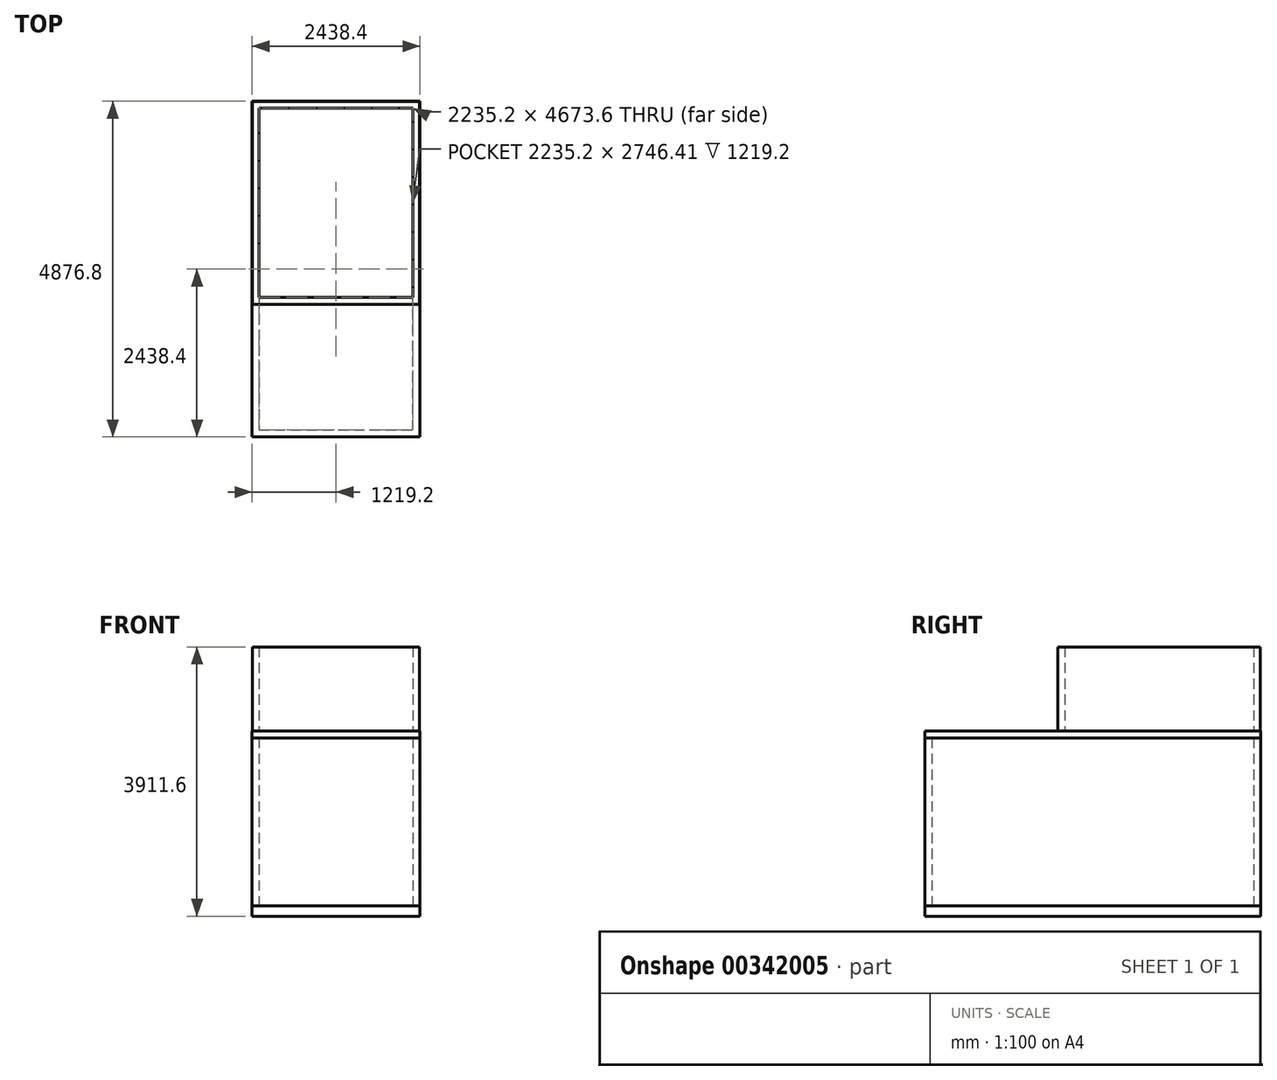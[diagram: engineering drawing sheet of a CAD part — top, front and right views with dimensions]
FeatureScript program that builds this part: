
annotation { "Feature Type Name" : "Feature", "Feature Type Description" : "" }
export const myFeature = defineFeature(function(context is Context, id is Id, definition is map)
    precondition{}
    {
        {
            var Q0;
            Q0=qCreatedBy(makeId("Top.planeOp"),FACE);
            var sketch = newSketch(context, id + "F0", { "sketchPlane" : qUnion([Q0])});
            skLineSegment(sketch, "E0.bottom", {"start": v(0, 0) * mm, "end": v(2438.4, 0) * mm});
            skLineSegment(sketch, "E0.top", {"start": v(0, 4876.8) * mm, "end": v(2438.4, 4876.8) * mm});
            skLineSegment(sketch, "E0.left", {"start": v(0, 0) * mm, "end": v(0, 4876.8) * mm});
            skLineSegment(sketch, "E0.right", {"start": v(2438.4, 0) * mm, "end": v(2438.4, 4876.8) * mm});
            skSolve(sketch);
        }
        {
            var Q0;
            Q0=makeQuery(id+"F0.imprint","IMPRINT",FACE,{"disambiguationData":[TD([[makeQuery(id+"F0.imprint","IMPRINT",EDGE,{"derivedFrom":sQuery(id+"F0.wireOp",EDGE,"E0.bottom")}),1.0]])]});
            extrude(context, id + "F1", {"entities" : qUnion([Q0]), "depth" : 152.4 * mm});
        }
        {
            var Q0;
            Q0=makeQuery(id+"F1.opExtrude","CAP_FACE",FACE,{"disambiguationData":[OSD([sQuery(id+"F0.wireOp",EDGE,"E0.bottom"),sQuery(id+"F0.wireOp",EDGE,"E0.top"),sQuery(id+"F0.wireOp",EDGE,"E0.left"),sQuery(id+"F0.wireOp",EDGE,"E0.right")])],"isStart":false});
            var sketch = newSketch(context, id + "F2", { "sketchPlane" : qUnion([Q0])});
            skLineSegment(sketch, "E1.0", {"start": v(2336.8, 4775.2) * mm, "end": v(101.6, 4775.2) * mm});
            skLineSegment(sketch, "E1.1", {"start": v(2336.8, 101.6) * mm, "end": v(2336.8, 4775.2) * mm});
            skLineSegment(sketch, "E1.2", {"start": v(101.6, 101.6) * mm, "end": v(2336.8, 101.6) * mm});
            skLineSegment(sketch, "E1.3", {"start": v(101.6, 4775.2) * mm, "end": v(101.6, 101.6) * mm});
            skSolve(sketch);
        }
        {
            var Q0;
            Q0=makeQuery(id+"F2.imprint","IMPRINT",FACE,{"disambiguationData":[TD([[makeQuery(id+"F2.imprint","IMPRINT",EDGE,{"derivedFrom":sQuery(id+"F2.wireOp",EDGE,"E1.0")}),-1.0]])]});
            extrude(context, id + "F3", {"entities" : qUnion([Q0]), "depth" : 2438.4 * mm});
        }
        {
            var Q0;
            Q0=makeQuery(id+"F3.opExtrude","CAP_FACE",FACE,{"disambiguationData":[OSD([sQuery(id+"F0.wireOp",EDGE,"E0.bottom"),sQuery(id+"F0.wireOp",EDGE,"E0.top"),sQuery(id+"F0.wireOp",EDGE,"E0.left"),sQuery(id+"F0.wireOp",EDGE,"E0.right"),sQuery(id+"F2.wireOp",EDGE,"E1.0"),sQuery(id+"F2.wireOp",EDGE,"E1.1"),sQuery(id+"F2.wireOp",EDGE,"E1.2"),sQuery(id+"F2.wireOp",EDGE,"E1.3")])],"isStart":false});
            var sketch = newSketch(context, id + "F4", { "sketchPlane" : qUnion([Q0])});
            skLineSegment(sketch, "E2.bottom", {"start": v(2438.4, 4876.8) * mm, "end": v(0, 4876.8) * mm});
            skLineSegment(sketch, "E2.top", {"start": v(2438.4, 0) * mm, "end": v(0, 0) * mm});
            skLineSegment(sketch, "E2.left", {"start": v(2438.4, 4876.8) * mm, "end": v(2438.4, 0) * mm});
            skLineSegment(sketch, "E2.right", {"start": v(0, 4876.8) * mm, "end": v(0, 0) * mm});
            skSolve(sketch);
        }
        {
            var Q0;
            Q0 = qSketchRegion(id + "F4", true);
            extrude(context, id + "F5", {"entities" : qUnion([Q0]), "depth" : 101.6 * mm});
        }
        {
            var Q0;
            Q0=makeQuery(id+"F5.opExtrude","CAP_FACE",FACE,{"disambiguationData":[OSD([sQuery(id+"F4.wireOp",EDGE,"E2.bottom"),sQuery(id+"F4.wireOp",EDGE,"E2.top"),sQuery(id+"F4.wireOp",EDGE,"E2.left"),sQuery(id+"F4.wireOp",EDGE,"E2.right")])],"isStart":false});
            var sketch = newSketch(context, id + "F6", { "sketchPlane" : qUnion([Q0])});
            skLineSegment(sketch, "E3.bottom", {"start": v(2438.4, 4876.8) * mm, "end": v(0, 4876.8) * mm});
            skLineSegment(sketch, "E3.top", {"start": v(2438.4, 1927.19) * mm, "end": v(0, 1927.19) * mm});
            skLineSegment(sketch, "E3.left", {"start": v(2438.4, 4876.8) * mm, "end": v(2438.4, 1927.19) * mm});
            skLineSegment(sketch, "E3.right", {"start": v(0, 4876.8) * mm, "end": v(0, 1927.19) * mm});
            skLineSegment(sketch, "E4.0", {"start": v(2336.8, 2028.79) * mm, "end": v(101.6, 2028.79) * mm});
            skLineSegment(sketch, "E4.1", {"start": v(2336.8, 4775.2) * mm, "end": v(2336.8, 2028.79) * mm});
            skLineSegment(sketch, "E4.2", {"start": v(2336.8, 4775.2) * mm, "end": v(101.6, 4775.2) * mm});
            skLineSegment(sketch, "E4.3", {"start": v(101.6, 4775.2) * mm, "end": v(101.6, 2028.79) * mm});
            skLineSegment(sketch, "E5.0", {"start": v(2432.05, 4870.45) * mm, "end": v(6.35, 4870.45) * mm});
            skLineSegment(sketch, "E5.1", {"start": v(2432.05, 6.35) * mm, "end": v(2432.05, 4870.45) * mm});
            skLineSegment(sketch, "E5.2", {"start": v(6.35, 6.35) * mm, "end": v(2432.05, 6.35) * mm});
            skLineSegment(sketch, "E5.3", {"start": v(6.35, 4870.45) * mm, "end": v(6.35, 6.35) * mm});
            skSolve(sketch);
        }
        {
            var Q0;
            Q0=makeQuery(id+"F6.imprint","IMPRINT",FACE,{"disambiguationData":[TD([[makeQuery(id+"F6.imprint","IMPRINT",EDGE,{"derivedFrom":sQuery(id+"F6.wireOp",EDGE,"E4.0")}),1.0]])]});
            extrude(context, id + "F7", {"entities" : qUnion([Q0]), "operationType" : NewBodyOperationType.ADD, "depth" : 1219.2 * mm});
        }
    });
